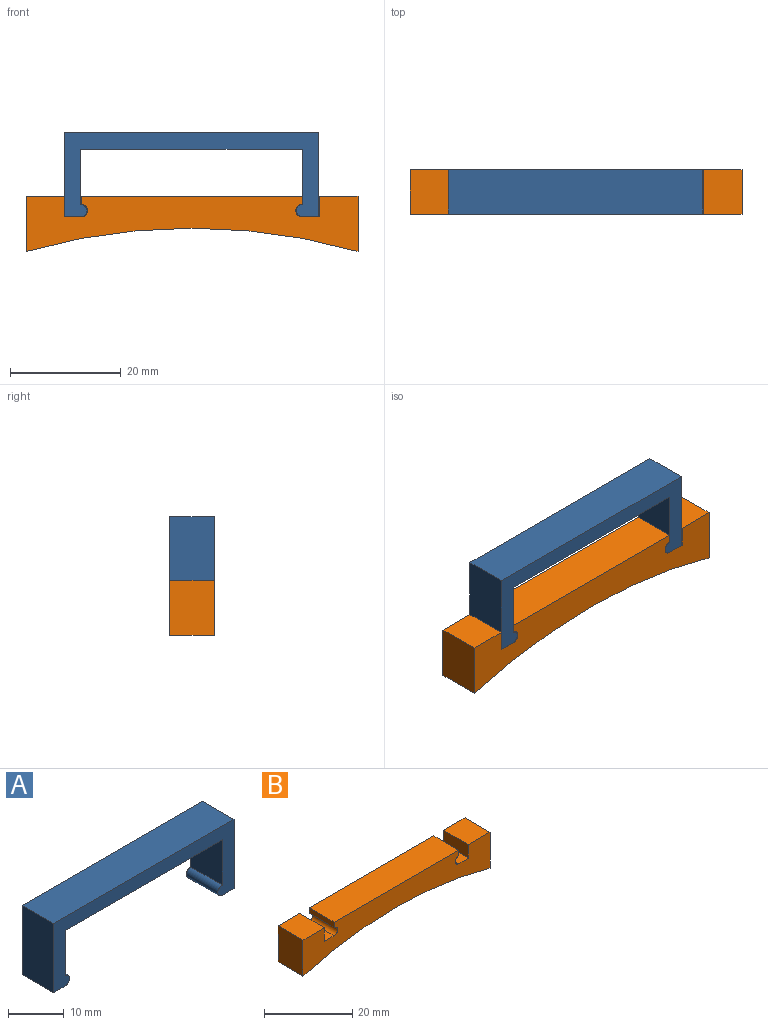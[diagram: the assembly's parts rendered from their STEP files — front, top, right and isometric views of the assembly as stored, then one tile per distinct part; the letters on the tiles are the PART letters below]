
ASSEMBLY  parts=2 mates=1
PART A: 12 faces, bbox 46x8x15.3 mm
  f0: plane 46x8mm, normal (0,0,1), area 368mm2, adj f1,f9,f10,f11
  f1: plane 15.25x8mm, normal (-1,0,0), area 122mm2, adj f0,f2,f10,f11
  f2: plane 8x3mm, normal (0,0,-1), area 24mm2, adj f1,f3,f10,f11
  f3: cylinder r=1.12mm len=8mm, axis (0,1,0), area 28.3mm2, adj f2,f4,f10,f11
  f4: plane 10x8mm, normal (1,0,0), area 80mm2, adj f3,f5,f10,f11
  f5: plane 40x8mm, normal (0,0,-1), area 320mm2, adj f4,f6,f10,f11
  f6: plane 10x8mm, normal (-1,0,0), area 80mm2, adj f5,f7,f10,f11
  f7: cylinder r=1.12mm len=8mm, axis (0,1,0), area 28.3mm2, adj f6,f8,f10,f11
  f8: plane 8x3mm, normal (0,0,-1), area 24mm2, adj f7,f9,f10,f11
  f9: plane 15.25x8mm, normal (1,0,0), area 122mm2, adj f0,f8,f10,f11
  f10: plane 46x15.25mm, normal (0,-1,0), area 215.5mm2, adj f0,f1,f2,f3,f4,f5,f6,f7
  f11: plane 46x15.25mm, normal (0,1,0), area 215.5mm2, adj f0,f1,f2,f3,f4,f5,f6,f7
PART B: 16 faces, bbox 60x8x10 mm
  f0: plane 8x6.9mm, normal (0,0,1), area 55.2mm2, adj f2,f4,f5,f15
  f1: plane 40x8mm, normal (0,0,1), area 320mm2, adj f2,f5,f11,f12
  f2: plane 60x10mm, normal (0,-1,0), area 403.6mm2, adj f0,f1,f3,f4,f6,f7,f8,f9
  f3: plane 10x8mm, normal (-1,0,0), area 80mm2, adj f2,f5,f6,f7
  f4: plane 10x8mm, normal (1,0,0), area 80mm2, adj f0,f2,f5,f7
  f5: plane 60x10mm, normal (0,1,0), area 403.6mm2, adj f0,f1,f3,f4,f6,f7,f8,f9
  f6: plane 8x6.9mm, normal (0,0,1), area 55.2mm2, adj f2,f3,f5,f8
  f7: cylinder r=109mm len=60mm, axis (0,-1,0), area 486.3mm2, adj f2,f3,f4,f5
  f8: plane 8x3.76mm, normal (1,0,0), area 30.1mm2, adj f2,f5,f6,f9
  f9: plane 8x3.1mm, normal (0,0,1), area 24.8mm2, adj f2,f5,f8,f10
  f10: cylinder r=1.13mm len=8mm, axis (0,-1,0), area 28.4mm2, adj f2,f5,f9,f11
  f11: plane 8x1.5mm, normal (-1,0,0), area 12mm2, adj f1,f2,f5,f10
  f12: plane 8x1.5mm, normal (1,0,0), area 12mm2, adj f1,f2,f5,f13
  f13: cylinder r=1.13mm len=8mm, axis (0,-1,0), area 28.4mm2, adj f2,f5,f12,f14
  f14: plane 8x3.1mm, normal (0,0,1), area 24.8mm2, adj f2,f5,f13,f15
  f15: plane 8x3.76mm, normal (-1,0,0), area 30.1mm2, adj f0,f2,f5,f14
PLACE A t=(-17.75,3.74,-10.31)mm
PLACE B t=(-10.65,3.96,-3.47)mm
MATE slider A.f10 <-> B.f2  axis (0,-1,0) through (-42.71,-4.26,2.77)mm
